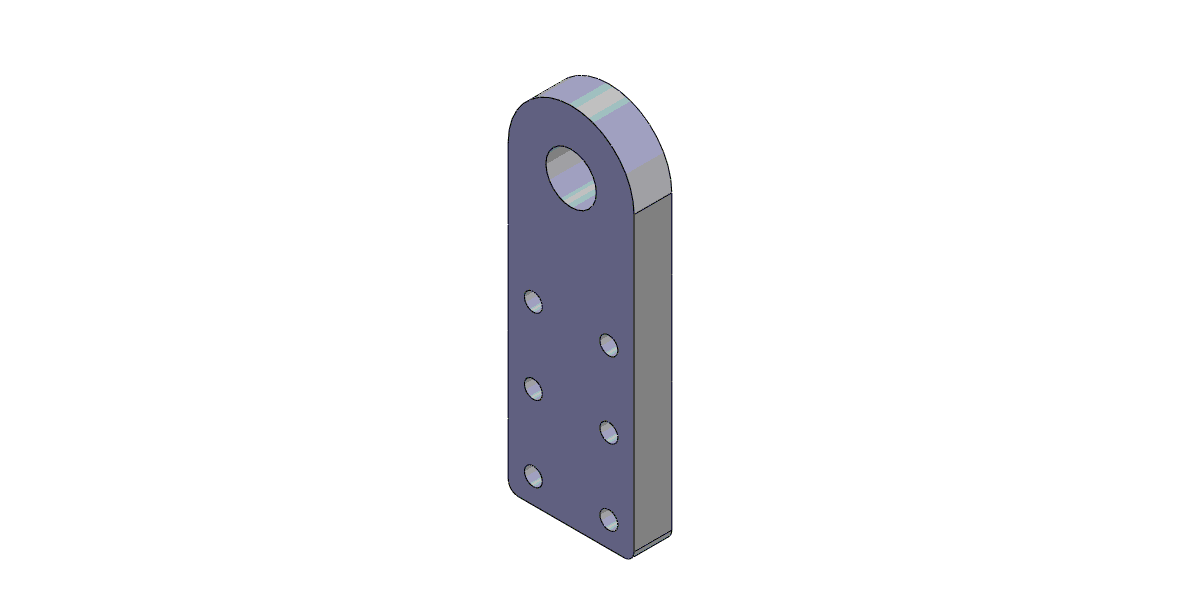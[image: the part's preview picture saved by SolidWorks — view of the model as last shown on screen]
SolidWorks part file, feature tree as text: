
SOLIDWORKS PART (.sldprt)
format: sldprt  version: not decoded by parser v0  size: 177,664 bytes
history: native  units: mm
features: sketch x5, hole x2, material x1, extrude x1, fillet x1 (+13 scaffold rows collapsed)
feature tree (23):
  scaffold x13  (default folders/planes/origin — collapsed)
  material  "7079 Alloy"
  sketch  "Sketch1"  dims[D2=76.2mm D1=0.0mm]
  extrude  "Boss-Extrude1"  Depth=9.525mm
  fillet  "Fillet1"  Radius=2.54mm
  hole  "1/2 (0.5) Diameter Hole1"  Diameter=12.7mm Depth=9.525mm
  sketch  "Sketch3"
  sketch  "Sketch2"  dims[hole-wizard template sketch: 61 standard entries collapsed; hole parameters above]
  hole  "#8 Clearance Hole1"  Diameter=4.4958mm Depth=9.525mm
  sketch  "Sketch4"
  sketch  "Sketch5"  dims[Thru Hole Dia.=4.4958mm Thru Hole Depth=9.525mm]
decode coverage: 7 of 9 modeling features carry decoded parameters
note: ~ marks probable driven/reference dimensions
note: suppression state not decoded; provenance and decode notes live in map.json
